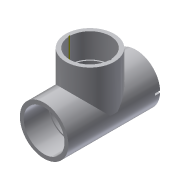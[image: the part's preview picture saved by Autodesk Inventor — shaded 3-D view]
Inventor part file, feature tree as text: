
AUTODESK INVENTOR PART (.ipt)
format: ipt  version: 2016 (Build 200138000, 138)  size: 201,728 bytes
history: native  units: in
note: dims shown in document units (in); Inventor stores cm internally (conversion verified against a paired STEP export)
features: sketch x10, extrude x9, plane x2
ambient origin geometry x8: Origin, YZ Plane, XZ Plane, XY Plane, X Axis, Y Axis, Z Axis, Center Point
bodies: Solid1 (feature_tree)
feature tree (21):
  extrude  "mainBody"  Depth=5.5906in TaperAngle=0.0deg
  sketch  "Sketch10"  dims[d29=2.7953in d30=2.9528in]
  plane  "Work Plane5"
  extrude  "TBody"  Depth=2.7953in
  extrude  "TSocket"  Depth=1.25in
  extrude  "TTube"  Depth=1.4961in
  extrude  "mainTube"  Depth=1.5in
  extrude  "mainSocket1"  Depth=2.4803in
  extrude  "mainSocket2"  Depth=1.4961in
  extrude  "Extrusion20"  Depth=1.4961in
  plane  "Work Plane6"
  extrude  "Extrusion22"  Depth=0.1in
  sketch  "Sketch1"  dims[d0=2.9528in d1=5.5906in d2=0.0in]
  sketch  "Sketch11"  dims[d31=1.4961in d32=1.25in d33=0.0in d34=0.0in d35=2.4803in]
  sketch  "Sketch12"  dims[d37=1.4961in d38=0.0in d39=2.3228in]
  sketch  "Sketch13"  dims[d41=1.5in d42=0.0in d43=2.3228in]
  sketch  "Sketch14"  dims[d45=7.0in d46=0.0in d47=2.4803in]
  sketch  "Sketch15"  dims[d49=1.4961in d50=0.0in d51=2.4803in]
  sketch  "Sketch16"  dims[d53=1.4961in d54=0.0in d72=0.1575in]
  sketch  "Sketch24"  dims[d73=1.4961in d74=0.0in d75=0.1in]
  sketch  "Sketch27"  dims[d76=1.2598in d79=1.0in d80=0.0in]
